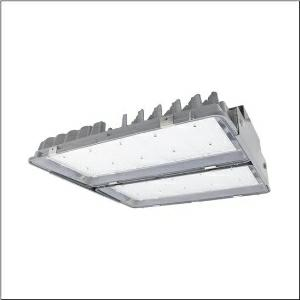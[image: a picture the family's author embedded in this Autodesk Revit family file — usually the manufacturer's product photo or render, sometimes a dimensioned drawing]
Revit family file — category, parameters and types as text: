
# Revit family: highbay_11xtreme_51hf62db4tma
name_source: partatom
category: Lighting Fixtures
units: mm (PartAtom-declared; Revit-internal decimal feet)

## family parameters
Cut with Voids When Loaded = No
Host = Face
Light Source = No
Part Type = Normal
Room Calculation Point = No
Round Connector Dimension = Use Diameter
Shared = No

## types (1)
- --- (1 x LED, 54000 lm, 285.7 W, 4000K)
    Apparent Load = 286 VA
    CIE Flux Codes = 84 96 100 100 100
    Color Rendering = 80
    Color Temperature = 4000K
    Default Elevation = 1800 mm
    Description = Highbay 11Xtreme, high bay luminaire, primary light control with lens, of PMMA, primary optical cover: cover, of toughened safety glass, light emission: direct distribution, primary light characteristic: symmetric, installation type: suspended mounting, surface-mounted, 2x LED module,for 1x 2x LED, rated luminous flux: 54.000lm, luminous efficacy: 189lm/W, light colour: 840, colour temperature: 4000K, control gear: DALI 2, with cable H07RN-F 5x 1.5mm², mains connection: 220..240V, AC, 50/60Hz, cable length: 1,5m, rated input power: 286W, luminaire housing, of diecast aluminium, coated, silver, length: 595mm, width: 560mm, height: 195mm, protection rating (complete): IP66, insulation class (complete): insulation class I (protective earthing), certification: CE, ENEC, UKCA, protection symbol: D, ball protection: ball impact resistant according to DIN VDE 0710 part 13 (with chain suspension), impact resistance: IK08, permissible operating ambient temperature: -25..+60°C, reducing of maximum allowable ambient temperature of 5°C with ceiling mounting, packaging unit: 1 piece
    Height = 157 mm
    Lamp = 1 x LED
    Lamp Light Flux = 54000 lm
    Lamp Power = 285.7 W
    Lamp count = 1
    Length = 593 mm
    Luminous efficacy = 189 lm/W
    Manufacturer = Siteco
    ModVariant = No
    Model = 51HF62DB4TMA
    Mounting Place = Ceiling
    Mounting Type = Pendant
    Number of Poles = 1
    OnlyDefault = Yes
    Power Factor = 1
    Product Name = Highbay 11Xtreme
    Product group = high bay luminaire
    ProductGroupID = 901
    Protection Class = Protection class I
    Protection Degree = IP 66
    RLX_Detail_Level = 1
    RLX_Emergency_Light_Flux = 0 lm
    RLX_Emergency_Type = 0
    RLX_Emergency_Type_DB = No
    RlxData = <blob elided: 34293 chars, md5=8fb55ffb>
    Socket = socket
    Standby Power = 0 W
    System Light Flux = 54000 lm
    System Power = 286 W
    Type Comments = factory setting: luminous flux: 100 % | dim-lin: 254 | 970 mA
    Type Image = l_1258340.jpg
    URL = http://relux.com
    VarID = @adj_083110
    Voltage = 0 V
    Weight = 0.00 kg
    Width = 568 mm

## geometry (parser evidence)
native form markers: Blend x4, Sweep x12
no freeform markers — native parametric forms only
